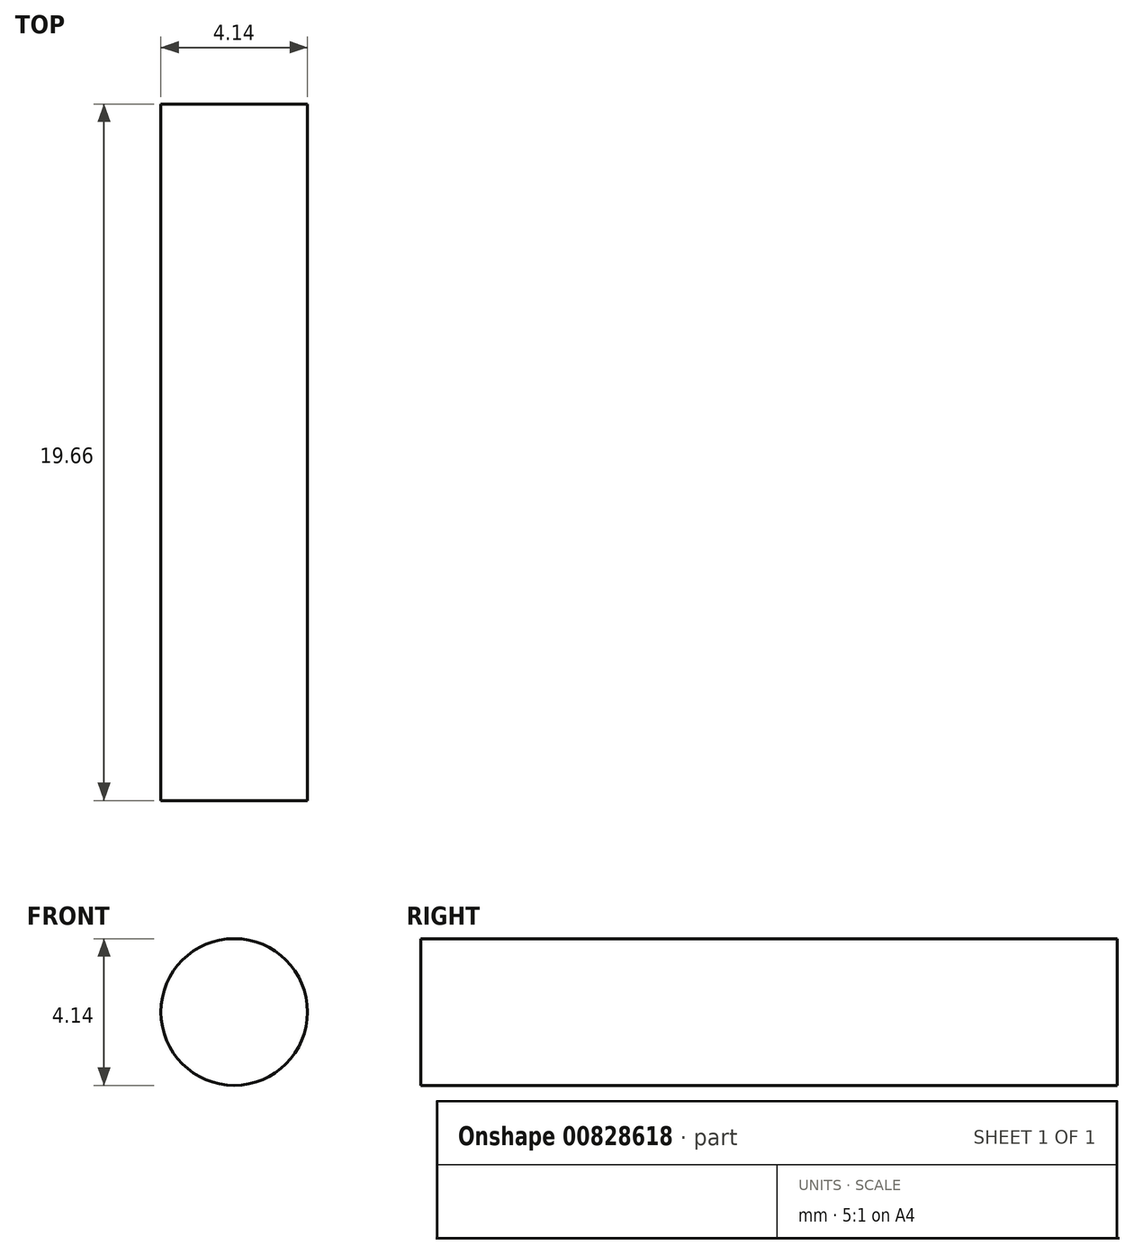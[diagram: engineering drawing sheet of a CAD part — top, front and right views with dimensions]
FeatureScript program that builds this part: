
annotation { "Feature Type Name" : "Feature", "Feature Type Description" : "" }
export const myFeature = defineFeature(function(context is Context, id is Id, definition is map)
    precondition{}
    {
        {
            var Q0;
            Q0=qCreatedBy(makeId("Front.planeOp"),FACE);
            var sketch = newSketch(context, id + "F0", { "sketchPlane" : qUnion([Q0])});
            skCircle(sketch, "E0", {"center": v(0, 0) * mm, "radius": 2.07 * mm});
            skSolve(sketch);
        }
        {
            var Q0;
            Q0 = qSketchRegion(id + "F0", true);
            extrude(context, id + "F1", {"entities" : qUnion([Q0]), "endBound" : BoundingType.SYMMETRIC, "depth" : 19.66 * mm, "offsetDistance" : 25.4 * mm});
        }
    });
